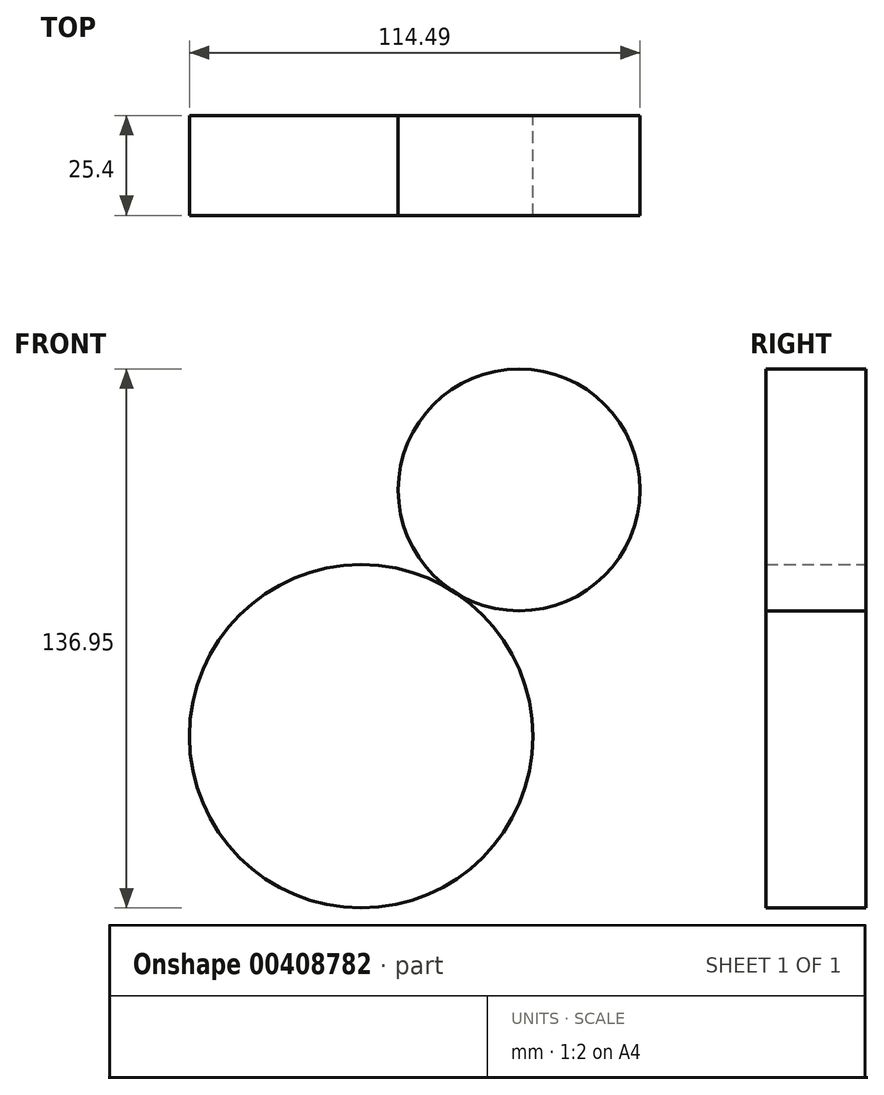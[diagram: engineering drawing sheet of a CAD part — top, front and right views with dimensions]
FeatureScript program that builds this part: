
annotation { "Feature Type Name" : "Feature", "Feature Type Description" : "" }
export const myFeature = defineFeature(function(context is Context, id is Id, definition is map)
    precondition{}
    {
        {
            var Q0;
            Q0=qCreatedBy(makeId("Front.planeOp"),FACE);
            var sketch = newSketch(context, id + "F0", { "sketchPlane" : qUnion([Q0])});
            skCircle(sketch, "E0", {"center": v(14.05, 0) * mm, "radius": 43.63 * mm});
            skCircle(sketch, "E1", {"center": v(54.19, 62.6) * mm, "radius": 30.73 * mm});
            skSolve(sketch);
        }
        {
            var Q0;
            Q0=makeQuery(id+"F0.imprint","IMPRINT",FACE,{"disambiguationData":[TD([[makeQuery(id+"F0.imprint","IMPRINT",EDGE,{"derivedFrom":sQuery(id+"F0.wireOp",EDGE,"E0")}),1.0]])]});
            var Q1;
            Q1=makeQuery(id+"F0.imprint","IMPRINT",FACE,{"disambiguationData":[TD([[makeQuery(id+"F0.imprint","IMPRINT",EDGE,{"derivedFrom":sQuery(id+"F0.wireOp",EDGE,"E1")}),1.0]])]});
            extrude(context, id + "F1", {"entities" : qUnion([Q0, Q1]), "depth" : 25.4 * mm});
        }
    });
